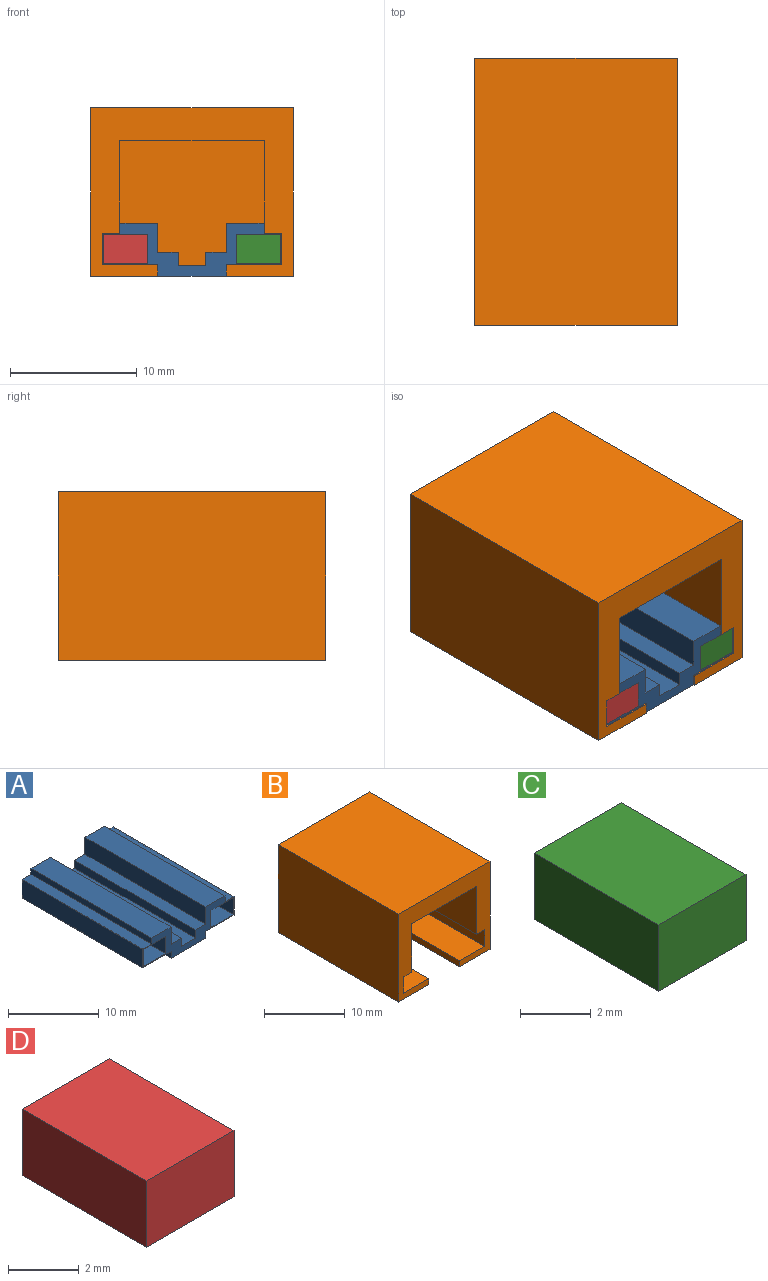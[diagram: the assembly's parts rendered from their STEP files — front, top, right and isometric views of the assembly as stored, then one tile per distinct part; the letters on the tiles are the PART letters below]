
ASSEMBLY  parts=4 mates=3
PART A: 30 faces, bbox 14.2x18.8x4.2 mm
  f0: plane 14.2x4.2mm, normal (0,1,0), area 18.6mm2, adj f1,f2,f3,f4,f5,f6,f7,f8
  f1: plane 18.8x0.8mm, normal (1,0,0), area 15mm2, adj f0,f2,f28,f29
  f2: plane 18.8x3mm, normal (0,0,1), area 56.4mm2, adj f0,f1,f3,f29
  f3: plane 18.8x2.3mm, normal (-1,0,0), area 43.2mm2, adj f0,f2,f4,f29
  f4: plane 18.8x1.6mm, normal (0,0,1), area 30.1mm2, adj f0,f3,f5,f29
  f5: plane 18.8x1.09mm, normal (-1,0,0), area 20.4mm2, adj f0,f4,f6,f29
  f6: plane 18.8x2.2mm, normal (0,0,1), area 41.4mm2, adj f0,f5,f7,f29
  f7: plane 18.8x1.09mm, normal (1,0,0), area 20.4mm2, adj f0,f6,f8,f29
  f8: plane 18.8x1.6mm, normal (0,0,1), area 30.1mm2, adj f0,f7,f9,f29
  f9: plane 18.8x2.3mm, normal (1,0,0), area 43.2mm2, adj f0,f8,f10,f29
  f10: plane 18.8x3mm, normal (0,0,1), area 56.4mm2, adj f0,f9,f11,f29
  f11: plane 18.8x0.8mm, normal (-1,0,0), area 15mm2, adj f0,f10,f12,f29
  f12: plane 18.8x1.4mm, normal (0,0,1), area 26.3mm2, adj f0,f11,f13,f29
  f13: plane 18.8x2.5mm, normal (-1,0,0), area 47mm2, adj f0,f12,f14,f29
  f14: plane 18.8x4.4mm, normal (0,0,-1), area 82.7mm2, adj f0,f13,f15,f29
  f15: plane 18.8x0.9mm, normal (-1,0,0), area 16.9mm2, adj f0,f14,f16,f29
  f16: plane 18.8x5.4mm, normal (0,0,-1), area 101.5mm2, adj f0,f15,f17,f29
  f17: plane 18.8x0.9mm, normal (1,0,0), area 16.9mm2, adj f0,f16,f18,f29
  f18: plane 18.8x4.4mm, normal (0,0,-1), area 82.7mm2, adj f0,f17,f19,f29
  f19: plane 18.8x2.5mm, normal (1,0,0), area 47mm2, adj f0,f18,f28,f29
  f20: plane 18.8x3.5mm, normal (0,0,1), area 65.8mm2, adj f0,f21,f26,f29
  f21: plane 18.8x2.3mm, normal (1,0,0), area 43.2mm2, adj f0,f20,f22,f29
  f22: plane 18.8x3.5mm, normal (0,0,-1), area 65.8mm2, adj f0,f21,f26,f29
  f23: plane 18.8x3.5mm, normal (0,0,-1), area 65.8mm2, adj f0,f24,f27,f29
  f24: plane 18.8x2.3mm, normal (-1,0,0), area 43.2mm2, adj f0,f23,f25,f29
  f25: plane 18.8x3.5mm, normal (0,0,1), area 65.8mm2, adj f0,f24,f27,f29
  f26: plane 18.8x2.3mm, normal (-1,0,0), area 43.2mm2, adj f0,f20,f22,f29
  f27: plane 18.8x2.3mm, normal (1,0,0), area 43.2mm2, adj f0,f23,f25,f29
  f28: plane 18.8x1.4mm, normal (0,0,1), area 26.3mm2, adj f0,f1,f19,f29
  f29: plane 14.2x4.2mm, normal (0,-1,0), area 18.6mm2, adj f1,f2,f3,f4,f5,f6,f7,f8
PART B: 18 faces, bbox 16x21.1x13.3 mm
  f0: plane 16x13.3mm, normal (0,-1,0), area 89.2mm2, adj f1,f3,f4,f5,f6,f7,f8,f9
  f1: plane 21.1x13.3mm, normal (1,0,0), area 280.6mm2, adj f0,f2,f4,f5
  f2: plane 16x13.3mm, normal (0,1,0), area 212.8mm2, adj f1,f3,f4,f5
  f3: plane 21.1x13.3mm, normal (-1,0,0), area 280.6mm2, adj f0,f2,f4,f5
  f4: plane 21.1x16mm, normal (0,0,1), area 337.6mm2, adj f0,f1,f2,f3
  f5: plane 21.1x16mm, normal (0,0,-1), area 235.5mm2, adj f0,f1,f2,f3,f6,f7,f17
  f6: plane 18.9x0.9mm, normal (1,0,0), area 17mm2, adj f0,f5,f16,f17
  f7: plane 18.9x0.9mm, normal (-1,0,0), area 17mm2, adj f0,f5,f8,f17
  f8: plane 18.9x4.4mm, normal (0,0,1), area 83.2mm2, adj f0,f7,f9,f17
  f9: plane 18.9x2.5mm, normal (-1,0,0), area 47.2mm2, adj f0,f8,f10,f17
  f10: plane 18.9x1.4mm, normal (0,0,-1), area 26.5mm2, adj f0,f9,f11,f17
  f11: plane 18.9x7.3mm, normal (-1,0,0), area 138mm2, adj f0,f10,f12,f17
  f12: plane 18.9x11.4mm, normal (0,0,-1), area 215.5mm2, adj f0,f11,f13,f17
  f13: plane 18.9x7.3mm, normal (1,0,0), area 138mm2, adj f0,f12,f14,f17
  f14: plane 18.9x1.4mm, normal (0,0,-1), area 26.5mm2, adj f0,f13,f15,f17
  f15: plane 18.9x2.5mm, normal (1,0,0), area 47.2mm2, adj f0,f14,f16,f17
  f16: plane 18.9x4.4mm, normal (0,0,1), area 83.2mm2, adj f0,f6,f15,f17
  f17: plane 14.2x10.7mm, normal (0,-1,0), area 123.6mm2, adj f5,f6,f7,f8,f9,f10,f11,f12
PART C: 6 faces, bbox 3.5x5x2.3 mm
  f0: plane 5x2.3mm, normal (1,0,0), area 11.5mm2, adj f1,f3,f4,f5
  f1: plane 5x3.5mm, normal (0,0,1), area 17.5mm2, adj f0,f2,f4,f5
  f2: plane 5x2.3mm, normal (-1,0,0), area 11.5mm2, adj f1,f3,f4,f5
  f3: plane 5x3.5mm, normal (0,0,-1), area 17.5mm2, adj f0,f2,f4,f5
  f4: plane 3.5x2.3mm, normal (0,1,0), area 8.1mm2, adj f0,f1,f2,f3
  f5: plane 3.5x2.3mm, normal (0,-1,0), area 8.1mm2, adj f0,f1,f2,f3
PART D: 6 faces, bbox 3.5x5x2.3 mm
  f0: plane 5x2.3mm, normal (-1,0,0), area 11.5mm2, adj f1,f3,f4,f5
  f1: plane 5x3.5mm, normal (0,0,-1), area 17.5mm2, adj f0,f2,f4,f5
  f2: plane 5x2.3mm, normal (1,0,0), area 11.5mm2, adj f1,f3,f4,f5
  f3: plane 5x3.5mm, normal (0,0,1), area 17.5mm2, adj f0,f2,f4,f5
  f4: plane 3.5x2.3mm, normal (0,1,0), area 8.1mm2, adj f0,f1,f2,f3
  f5: plane 3.5x2.3mm, normal (0,-1,0), area 8.1mm2, adj f0,f1,f2,f3
PLACE A at identity
PLACE B at identity
PLACE C at identity
PLACE D at identity
MATE fastened C.f5 <-> A.f29  axis (0,-1,0) through (5.26,-10.45,2.18)mm
MATE fastened D.f5 <-> A.f29  axis (0,-1,0) through (-5.26,-10.45,2.18)mm
MATE fastened A.f14 <-> B.f16  axis (0,0,-1) through (-7.1,8.35,0.9)mm
